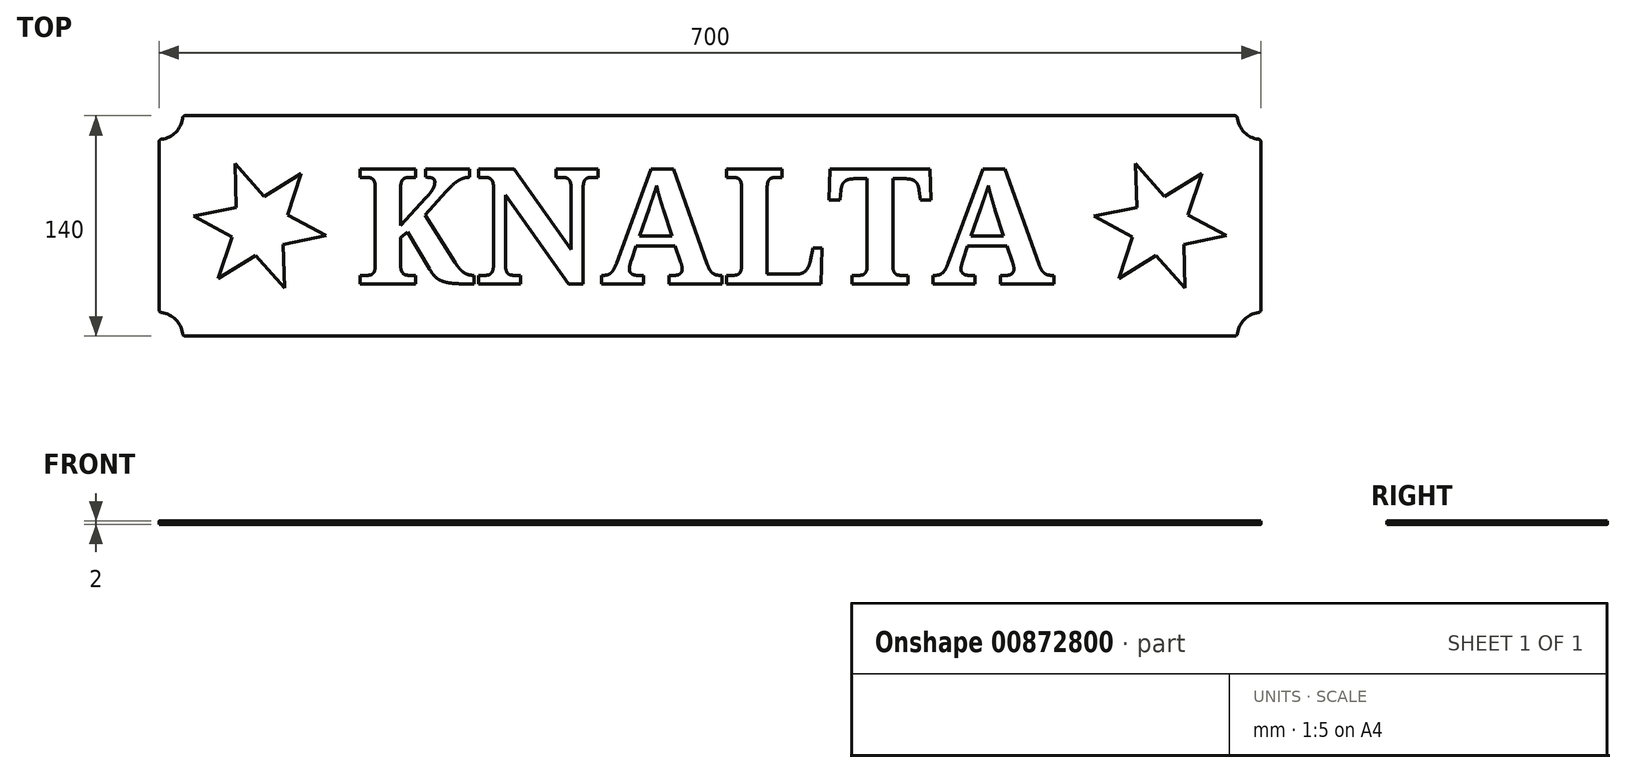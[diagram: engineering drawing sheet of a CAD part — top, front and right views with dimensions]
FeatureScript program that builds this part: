
annotation { "Feature Type Name" : "Feature", "Feature Type Description" : "" }
export const myFeature = defineFeature(function(context is Context, id is Id, definition is map)
    precondition{}
    {
        {
            var Q0;
            Q0=qCreatedBy(makeId("Top.planeOp"),FACE);
            var sketch = newSketch(context, id + "F0", { "sketchPlane" : qUnion([Q0])});
            skLineSegment(sketch, "E0", {"start": v(0, 459.17) * mm, "end": v(0, -526.61) * mm, "construction": true});
            skLineSegment(sketch, "E1", {"start": v(-506.97, 0) * mm, "end": v(534.36, 0) * mm, "construction": true});
            skLineSegment(sketch, "E2.bottom", {"start": v(-333.12, 70) * mm, "end": v(0, 70) * mm});
            skLineSegment(sketch, "E2.top", {"start": v(-350, 0) * mm, "end": v(0, 0) * mm});
            skLineSegment(sketch, "E2.left", {"start": v(-350, 53.12) * mm, "end": v(-350, 0) * mm});
            skLineSegment(sketch, "E2.right", {"start": v(0, 70) * mm, "end": v(0, 0) * mm});
            skArc(sketch, "E3", {"start": v(-348.24, 55.1) * mm, "mid": v(-339.4, 59.4) * mm, "end": v(-335.1, 68.24) * mm});
            skLineSegment(sketch, "E4.MirrorCS", {"start": v(350, 0) * mm, "end": v(0, 0) * mm});
            skLineSegment(sketch, "E5.MirrorCS", {"start": v(333.12, 70) * mm, "end": v(0, 70) * mm});
            skLineSegment(sketch, "E6.MirrorCS", {"start": v(350, 53.12) * mm, "end": v(350, 0) * mm});
            skArc(sketch, "E7.MirrorC", {"start": v(348.24, 55.1) * mm, "mid": v(339.4, 59.4) * mm, "end": v(335.1, 68.24) * mm});
            skLineSegment(sketch, "E8.MirrorCS", {"start": v(0, -70) * mm, "end": v(0, 0) * mm});
            skArc(sketch, "E9.MirrorC", {"start": v(-348.24, -55.1) * mm, "mid": v(-339.4, -59.4) * mm, "end": v(-335.1, -68.24) * mm});
            skLineSegment(sketch, "E10.MirrorCS", {"start": v(-333.12, -70) * mm, "end": v(0, -70) * mm});
            skLineSegment(sketch, "E11.MirrorCS", {"start": v(-350, -53.12) * mm, "end": v(-350, 0) * mm});
            skLineSegment(sketch, "E12.MirrorCS", {"start": v(350, -53.12) * mm, "end": v(350, 0) * mm});
            skLineSegment(sketch, "E13.MirrorCS", {"start": v(333.12, -70) * mm, "end": v(0, -70) * mm});
            skArc(sketch, "E14.MirrorC", {"start": v(348.24, -55.1) * mm, "mid": v(339.4, -59.4) * mm, "end": v(335.1, -68.24) * mm});
            skPoint(sketch, "E15.visualSharp", {"position": v(-335, 70) * mm});
            skArc(sketch, "E15.filletArc", {"start": v(-333.12, 70) * mm, "mid": v(-334.45, 69.5) * mm, "end": v(-335.1, 68.24) * mm});
            skPoint(sketch, "E16.visualSharp", {"position": v(-350, 55) * mm});
            skArc(sketch, "E16.filletArc", {"start": v(-348.24, 55.1) * mm, "mid": v(-349.5, 54.45) * mm, "end": v(-350, 53.12) * mm});
            skPoint(sketch, "E17.visualSharp", {"position": v(-350, -55) * mm});
            skArc(sketch, "E17.filletArc", {"start": v(-350, -53.12) * mm, "mid": v(-349.5, -54.45) * mm, "end": v(-348.24, -55.1) * mm});
            skPoint(sketch, "E18.visualSharp", {"position": v(-335, -70) * mm});
            skArc(sketch, "E18.filletArc", {"start": v(-335.1, -68.24) * mm, "mid": v(-334.45, -69.5) * mm, "end": v(-333.12, -70) * mm});
            skPoint(sketch, "E19.visualSharp", {"position": v(335, -70) * mm});
            skArc(sketch, "E19.filletArc", {"start": v(333.12, -70) * mm, "mid": v(334.45, -69.5) * mm, "end": v(335.1, -68.24) * mm});
            skPoint(sketch, "E20.visualSharp", {"position": v(350, -55) * mm});
            skArc(sketch, "E20.filletArc", {"start": v(348.24, -55.1) * mm, "mid": v(349.5, -54.45) * mm, "end": v(350, -53.12) * mm});
            skPoint(sketch, "E21.visualSharp", {"position": v(350, 55) * mm});
            skArc(sketch, "E21.filletArc", {"start": v(350, 53.12) * mm, "mid": v(349.5, 54.45) * mm, "end": v(348.24, 55.1) * mm});
            skPoint(sketch, "E22.visualSharp", {"position": v(335, 70) * mm});
            skArc(sketch, "E22.filletArc", {"start": v(335.1, 68.24) * mm, "mid": v(334.45, 69.5) * mm, "end": v(333.12, 70) * mm});
            skSolve(sketch);
        }
        {
            var Q0;
            Q0=qSketchRegion(id+"F0",true);
            extrude(context, id + "F1", {"entities" : qUnion([Q0]), "depth" : 2 * mm, "offsetDistance" : 25 * mm});
        }
        {
            var Q0;
            Q0=makeQuery(id+"F1.opExtrude","CAP_FACE",FACE,{"disambiguationData":[OSD([sQuery(id+"F0.wireOp",EDGE,"E2.bottom"),sQuery(id+"F0.wireOp",EDGE,"E2.left"),sQuery(id+"F0.wireOp",EDGE,"E3"),sQuery(id+"F0.wireOp",EDGE,"E5.MirrorCS"),sQuery(id+"F0.wireOp",EDGE,"E6.MirrorCS"),sQuery(id+"F0.wireOp",EDGE,"E7.MirrorC"),sQuery(id+"F0.wireOp",EDGE,"E9.MirrorC"),sQuery(id+"F0.wireOp",EDGE,"E10.MirrorCS"),sQuery(id+"F0.wireOp",EDGE,"E11.MirrorCS"),sQuery(id+"F0.wireOp",EDGE,"E12.MirrorCS"),sQuery(id+"F0.wireOp",EDGE,"E13.MirrorCS"),sQuery(id+"F0.wireOp",EDGE,"E14.MirrorC")])],"isStart":false});
            var sketch = newSketch(context, id + "F2", { "sketchPlane" : qUnion([Q0])});
            skPoint(sketch, "E23.0.midPoint", {"position": v(-257.12, -22.82) * mm});
            skLineSegment(sketch, "E24", {"start": v(-301.7, 39.5) * mm, "end": v(-300.89, 11.76) * mm});
            skLineSegment(sketch, "E25", {"start": v(-301.7, 39.5) * mm, "end": v(-283.26, 18.78) * mm});
            skLineSegment(sketch, "E26", {"start": v(-328.05, 6.14) * mm, "end": v(-303.63, -7.01) * mm});
            skLineSegment(sketch, "E27", {"start": v(-328.05, 6.14) * mm, "end": v(-300.89, 11.76) * mm});
            skLineSegment(sketch, "E28", {"start": v(-270.3, -39.5) * mm, "end": v(-271.11, -11.76) * mm});
            skLineSegment(sketch, "E29", {"start": v(-270.3, -39.5) * mm, "end": v(-288.74, -18.78) * mm});
            skLineSegment(sketch, "E30", {"start": v(-312.35, -33.35) * mm, "end": v(-288.74, -18.78) * mm});
            skLineSegment(sketch, "E31", {"start": v(-312.35, -33.35) * mm, "end": v(-303.63, -7.01) * mm});
            skLineSegment(sketch, "E32", {"start": v(-259.65, 33.35) * mm, "end": v(-283.26, 18.78) * mm});
            skLineSegment(sketch, "E33", {"start": v(-259.65, 33.35) * mm, "end": v(-268.37, 7.01) * mm});
            skLineSegment(sketch, "E34", {"start": v(-243.95, -6.14) * mm, "end": v(-268.37, 7.01) * mm});
            skLineSegment(sketch, "E35", {"start": v(-243.95, -6.14) * mm, "end": v(-271.11, -11.76) * mm});
            skPoint(sketch, "E36.center.orphan", {"position": v(-286, 0) * mm});
            skCircle(sketch, "E37", {"center": v(-286, 0) * mm, "radius": 18.98 * mm, "construction": true});
            skCircle(sketch, "E38", {"center": v(-286, 0) * mm, "radius": 42.5 * mm, "construction": true});
            skPoint(sketch, "E39.0.midPoint", {"position": v(314.88, -22.82) * mm});
            skLineSegment(sketch, "E40", {"start": v(270.3, 39.5) * mm, "end": v(271.11, 11.76) * mm});
            skLineSegment(sketch, "E41", {"start": v(270.3, 39.5) * mm, "end": v(288.74, 18.78) * mm});
            skLineSegment(sketch, "E42", {"start": v(243.95, 6.14) * mm, "end": v(268.37, -7.01) * mm});
            skLineSegment(sketch, "E43", {"start": v(243.95, 6.14) * mm, "end": v(271.11, 11.76) * mm});
            skLineSegment(sketch, "E44", {"start": v(301.7, -39.5) * mm, "end": v(300.89, -11.76) * mm});
            skLineSegment(sketch, "E45", {"start": v(301.7, -39.5) * mm, "end": v(283.26, -18.78) * mm});
            skLineSegment(sketch, "E46", {"start": v(259.65, -33.35) * mm, "end": v(283.26, -18.78) * mm});
            skLineSegment(sketch, "E47", {"start": v(259.65, -33.35) * mm, "end": v(268.37, -7.01) * mm});
            skLineSegment(sketch, "E48", {"start": v(312.35, 33.35) * mm, "end": v(288.74, 18.78) * mm});
            skLineSegment(sketch, "E49", {"start": v(312.35, 33.35) * mm, "end": v(303.63, 7.01) * mm});
            skLineSegment(sketch, "E50", {"start": v(328.05, -6.14) * mm, "end": v(303.63, 7.01) * mm});
            skLineSegment(sketch, "E51", {"start": v(328.05, -6.14) * mm, "end": v(300.89, -11.76) * mm});
            skPoint(sketch, "E52.center.orphan", {"position": v(286, 0) * mm});
            skCircle(sketch, "E53", {"center": v(286, 0) * mm, "radius": 18.98 * mm, "construction": true});
            skCircle(sketch, "E54", {"center": v(286, 0) * mm, "radius": 42.5 * mm, "construction": true});
            skText(sketch, "E55", { "text": "KNALTA", "fontName": "NotoSerif-Bold.ttf"});
            const initialGuessF2  = {"E55": [-0.225, -0.03685, 1, 0, 0.07365]};
            skSetInitialGuess(sketch, initialGuessF2);
            skSolve(sketch);
        }
        {
            var Q0;
            Q0=qSketchRegion(id+"F2",true);
            extrude(context, id + "F3", {"entities" : qUnion([Q0]), "operationType" : NewBodyOperationType.REMOVE, "oppositeDirection" : true, "depth" : 1 * mm, "offsetDistance" : 25 * mm});
        }
    });
